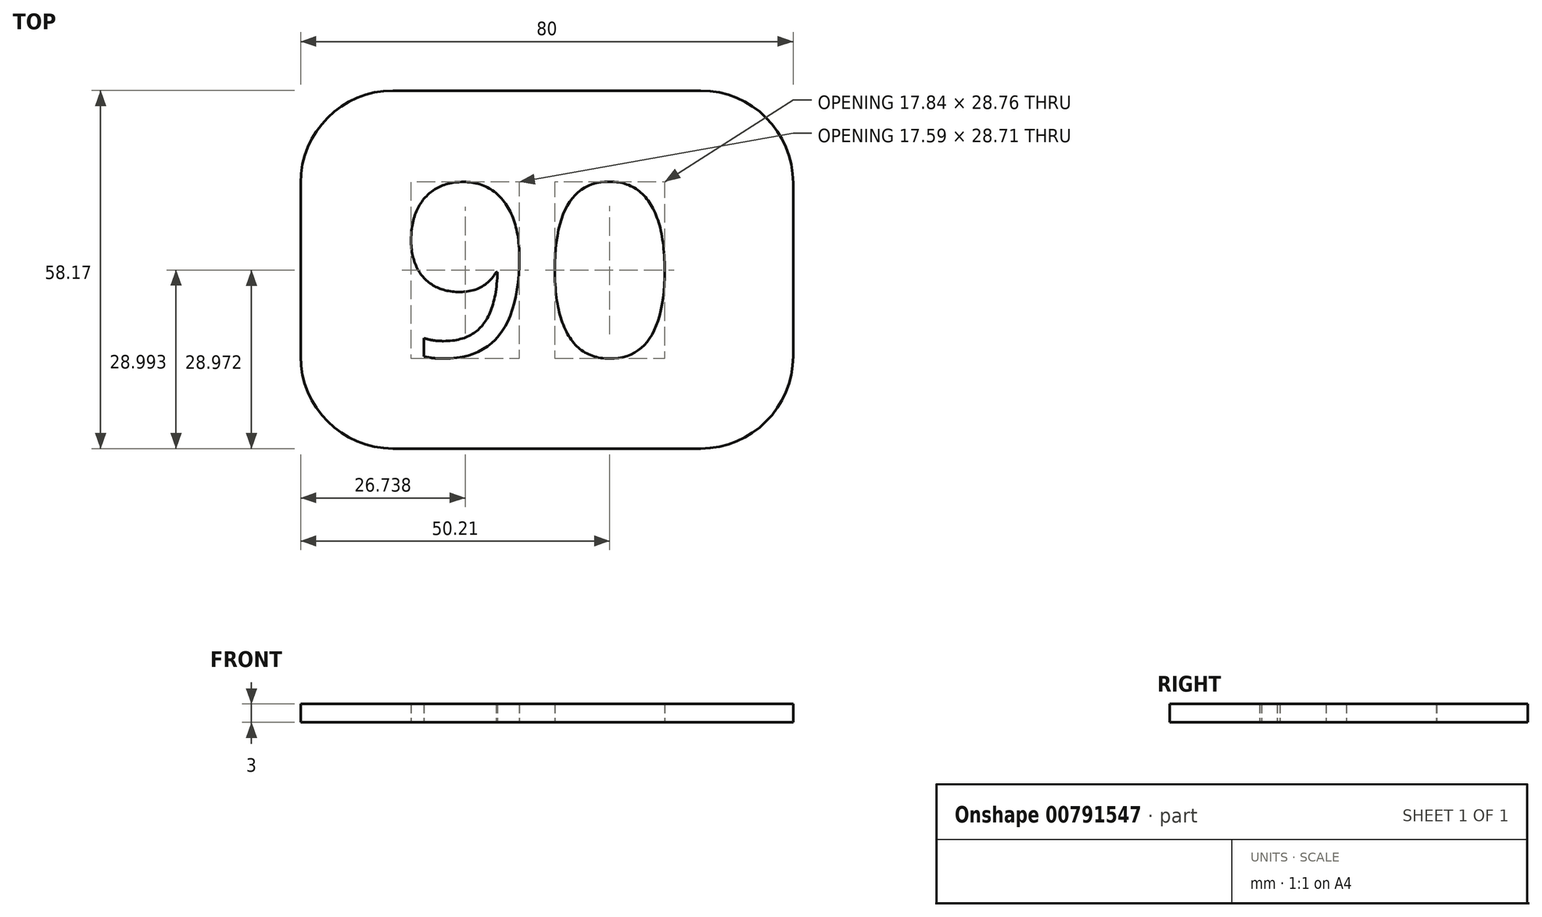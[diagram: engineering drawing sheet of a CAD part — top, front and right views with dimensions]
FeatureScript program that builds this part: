
annotation { "Feature Type Name" : "Feature", "Feature Type Description" : "" }
export const myFeature = defineFeature(function(context is Context, id is Id, definition is map)
    precondition{}
    {
        {
            var Q0;
            Q0=qCreatedBy(makeId("Top.planeOp"),FACE);
            var sketch = newSketch(context, id + "F0", { "sketchPlane" : qUnion([Q0])});
            skText(sketch, "E0", { "text": "90\n", "fontName": "DroidSansMono.ttf"});
            skLineSegment(sketch, "E1.bottom", {"start": v(-18.82, 28.9) * mm, "end": v(31.18, 28.9) * mm});
            skLineSegment(sketch, "E1.top", {"start": v(-18.82, -29.27) * mm, "end": v(31.18, -29.27) * mm});
            skLineSegment(sketch, "E1.left", {"start": v(-33.82, 13.9) * mm, "end": v(-33.82, -14.27) * mm});
            skLineSegment(sketch, "E1.right", {"start": v(46.18, 13.9) * mm, "end": v(46.18, -14.27) * mm});
            skPoint(sketch, "E2.visualSharp", {"position": v(-33.82, 28.9) * mm});
            skArc(sketch, "E2.filletArc", {"start": v(-18.82, 28.9) * mm, "mid": v(-29.43, 24.5) * mm, "end": v(-33.82, 13.9) * mm});
            skPoint(sketch, "E3.visualSharp", {"position": v(46.18, 28.9) * mm});
            skArc(sketch, "E3.filletArc", {"start": v(46.18, 13.9) * mm, "mid": v(41.79, 24.5) * mm, "end": v(31.18, 28.9) * mm});
            skPoint(sketch, "E4.visualSharp", {"position": v(46.18, -29.27) * mm});
            skArc(sketch, "E4.filletArc", {"start": v(31.18, -29.27) * mm, "mid": v(41.79, -24.88) * mm, "end": v(46.18, -14.27) * mm});
            skPoint(sketch, "E5.visualSharp", {"position": v(-33.82, -29.27) * mm});
            skArc(sketch, "E5.filletArc", {"start": v(-33.82, -14.27) * mm, "mid": v(-29.43, -24.88) * mm, "end": v(-18.82, -29.27) * mm});
            skPoint(sketch, "E6", {"position": v(6.18, 21.63) * mm});
            skPoint(sketch, "E7", {"position": v(6.18, -22.61) * mm});
            const initialGuessF0  = {"E0": [-0.01882, -0.01427, 1, 0, 0.02817]};
            skSetInitialGuess(sketch, initialGuessF0);
            skSolve(sketch);
        }
        {
            var Q0;
            Q0=makeQuery(id+"F0.imprint","IMPRINT",FACE,{"disambiguationData":[TD([[makeQuery(id+"F0.imprint","IMPRINT",EDGE,{"derivedFrom":sQuery(id+"F0.wireOp",EDGE,"E0.sketch_text.stroke-0")}),1.0]])]});
            extrude(context, id + "F1", {"entities" : qUnion([Q0]), "depth" : 3 * mm, "offsetDistance" : 25 * mm});
        }
    });
